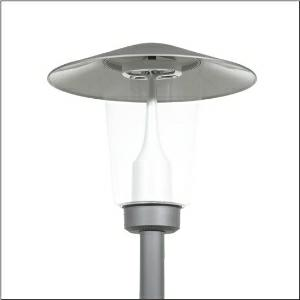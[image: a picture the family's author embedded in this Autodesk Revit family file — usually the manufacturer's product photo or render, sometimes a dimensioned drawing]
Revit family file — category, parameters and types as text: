
# Revit family: pilzleuchte_iq___p1_0a_5xa5235ff14hp_c3dc
name_source: partatom
category: Lighting Fixtures
units: mm (PartAtom-declared; Revit-internal decimal feet)

## family parameters
Cut with Voids When Loaded = No
Host = Face
Light Source = No
Part Type = Normal
Room Calculation Point = No
Round Connector Dimension = Use Diameter
Shared = No

## types (1)
- --- (1 x LED, 4740 lm, 33.6 W, 3000K)
    Apparent Load = 34 VA
    CIE Flux Codes = 35 64 90 96 100
    Color Rendering = 70
    Color Temperature = 3000K
    Default Elevation = 1800 mm
    Description = Mushroom Luminaire iQ, mast luminaire, Module 540 iQ-SR, primary light control with 3 zone facetted reflector, of plastic, silver coated, highly specular, structured, primary optical cover: cover, of PMMA, transparent, light distribution: P1.0a, light emission: direct distribution, primary light characteristic: strongly asymmetric, installation type: post-top, LED, High Power LED, rated luminous flux: 4.740lm, luminous efficacy: 141lm/W, light colour: 730, colour temperature: 3000K, control gear: iQ Street-Remote, control: pre-setting: logarithmic dimming characteristic, Street-Remote, Auto-Match, Temp-Guard, Lumen-Switch, Night-Set, Smart-Wire, Light-Fading, Desk-Remote (wireless, voltage-free reading and setting of iQ features in the workshop via application-optimized NFC function/RFID function), optimised constant luminous flux control (CLO 2.0), with terminal, 6-pole, max. 2.5mm², mains connection: 230..240V, AC, 50/60Hz, start of lifetime: 34W, end of service life: 36W, reduction: 15W, luminaire housing, upper part, of glass-fibre reinforced polyester, coated, Siteco® metallic grey (DB 702S), diameter: 650mm, height: 586mm, spigot size: d x l = 76 x 70mm (post-top) | with reducer (optional accessory) 60 x 70mm, mounting height: 3..5m, post-top mast mounting element, of diecast aluminium, coated, Siteco® metallic grey (DB 702S), Module 540 iQ-SR, traffic white (RAL 9016), equipment: Power, protection rating (complete): IP65, insulation class (complete): insulation class II (safety insulation), certification: CE, ENEC, VDE, packaging unit: 1 piece

Light Distribution: P1.0a
    Height = 586 mm
    Lamp = 1 x LED
    Lamp Light Flux = 4740 lm
    Lamp Power = 33.6 W
    Lamp count = 1
    Length = 650 mm
    Luminous efficacy = 141 lm/W
    Manufacturer = Siteco
    ModVariant = No
    Model = 5XA5235FF14HP
    Number of Poles = 1
    OnlyDefault = Yes
    Power Factor = 1
    Product Name = Pilzleuchte iQ | P1.0a
    Product group = mast luminaire | pylon top
    ProductGroupID = 6100
    Protection Class = Protection class II
    Protection Degree = IP 65
    RLX_Detail_Level = 1
    RLX_Emergency_Light_Flux = 0 lm
    RLX_Emergency_Type = 0
    RLX_Emergency_Type_DB = No
    RlxData = <blob elided: 51969 chars, md5=de1843e3>
    Socket = socket
    Standby Power = 0 W
    System Light Flux = 4740 lm
    System Power = 34 W
    Type Comments = factory setting: luminous flux: 100 % | dim-lin: 254 | 695 mA
    Type Image = l_1006077.jpg
    URL = http://relux.com
    VarID = @adj_189609
    Voltage = 0 V
    Weight = 0.00 kg
    Width = 0 mm  [stored 0 ft]

note: [stored X ft] marks values corroborated as IEEE doubles in the binary element streams (Revit-internal decimal feet)

## geometry (parser evidence)
native form markers: Blend x4, Sweep x12
no freeform markers — native parametric forms only
